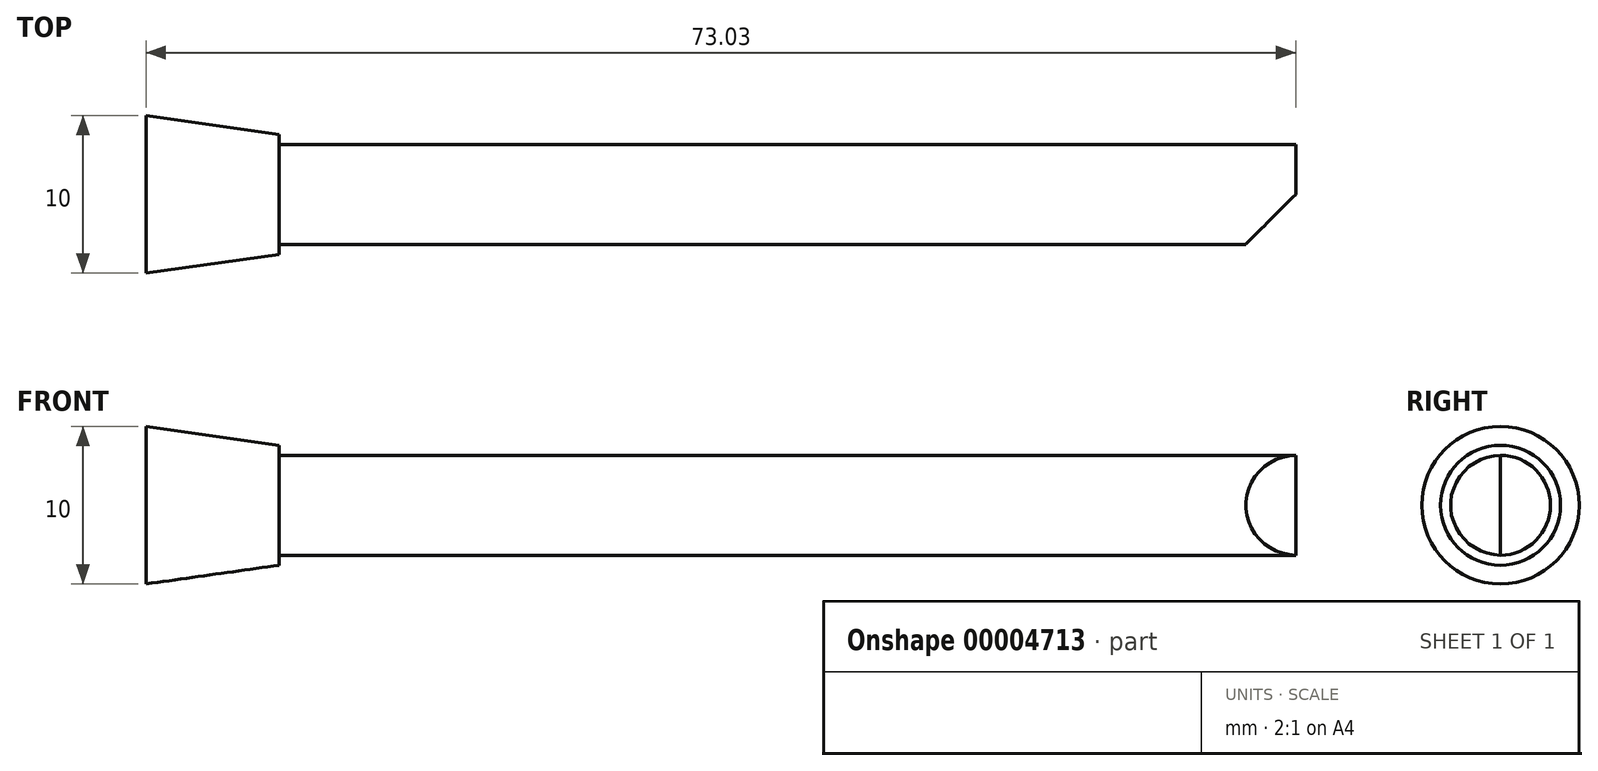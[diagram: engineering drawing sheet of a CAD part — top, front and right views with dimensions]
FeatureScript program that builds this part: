
annotation { "Feature Type Name" : "Feature", "Feature Type Description" : "" }
export const myFeature = defineFeature(function(context is Context, id is Id, definition is map)
    precondition{}
    {
        {
            var Q0;
            Q0=qCreatedBy(makeId("Top.planeOp"),FACE);
            var sketch = newSketch(context, id + "F0", { "sketchPlane" : qUnion([Q0])});
            skLineSegment(sketch, "E0.bottom", {"start": v(0, 0) * mm, "end": v(-76.2, 0) * mm});
            skLineSegment(sketch, "E0.top", {"start": v(0, 3.18) * mm, "end": v(-76.2, 3.18) * mm});
            skLineSegment(sketch, "E0.left", {"start": v(0, 0) * mm, "end": v(0, 3.18) * mm});
            skLineSegment(sketch, "E0.right", {"start": v(-76.2, 0) * mm, "end": v(-76.2, 3.18) * mm});
            skLineSegment(sketch, "E1.MirrorCS", {"start": v(-76.2, 0) * mm, "end": v(-76.2, -3.17) * mm});
            skLineSegment(sketch, "E2.MirrorCS", {"start": v(0, 0) * mm, "end": v(0, -3.17) * mm});
            skLineSegment(sketch, "E3.MirrorCS", {"start": v(0, -3.17) * mm, "end": v(-76.2, -3.17) * mm});
            skLineSegment(sketch, "E4", {"start": v(-67.73, 3.81) * mm, "end": v(-67.73, -3.81) * mm});
            skLineSegment(sketch, "E5", {"start": v(-67.73, -3.81) * mm, "end": v(-76.2, -5) * mm});
            skLineSegment(sketch, "E6", {"start": v(-76.2, -5) * mm, "end": v(-76.2, 5) * mm});
            skLineSegment(sketch, "E7", {"start": v(-76.2, 5) * mm, "end": v(-67.73, 3.81) * mm});
            skSolve(sketch);
        }
        {
            var Q0;
            Q0=makeQuery(id+"F0.imprint","IMPRINT",FACE,{"disambiguationData":[TD([[makeQuery(id+"F0.imprint","IMPRINT",EDGE,{"derivedFrom":sQuery(id+"F0.wireOp",EDGE,"E0.bottom")}),-1.0]])]});
            var Q1;
            {var subQ5=sQuery(id+"F0.wireOp",EDGE,"E7");Q1=makeQuery(id+"F0.imprint","IMPRINT",FACE,{"disambiguationData":[TD([[makeQuery(id+"F0.imprint","IMPRINT",EDGE,{"derivedFrom":subQ5}),-1.0]])]});}
            var Q2;
            Q2=sQuery(id+"F0.wireOp",EDGE,"E0.bottom");
            revolve(context, id + "F1", {"entities" : qUnion([Q0, Q1]), "axis" : qUnion([Q2]), "revolveType" : RevolveType.FULL});
        }
        {
            var Q0;
            Q0=qCreatedBy(makeId("Top.planeOp"),FACE);
            var sketch = newSketch(context, id + "F2", { "sketchPlane" : qUnion([Q0])});
            skLineSegment(sketch, "E8", {"start": v(0, 3.18) * mm, "end": v(-6.35, -3.17) * mm});
            skLineSegment(sketch, "E9", {"start": v(-6.35, -3.18) * mm, "end": v(0, -3.18) * mm});
            skLineSegment(sketch, "E10", {"start": v(0, -3.17) * mm, "end": v(0, 3.18) * mm});
            skLineSegment(sketch, "E11", {"start": v(-3.18, 0) * mm, "end": v(-3.18, 3.18) * mm});
            skLineSegment(sketch, "E12", {"start": v(-3.18, 3.18) * mm, "end": v(0, 3.18) * mm});
            skSolve(sketch);
        }
        {
            var Q0;
            Q0=makeQuery(id+"F2.imprint","IMPRINT",FACE,{"disambiguationData":[TD([[makeQuery(id+"F2.imprint","IMPRINT",EDGE,{"derivedFrom":sQuery(id+"F2.wireOp",EDGE,"E8")}),1.0]])]});
            var Q1;
            {var subQ2=sQuery(id+"F2.wireOp",EDGE,"E11");Q1=makeQuery(id+"F2.imprint","IMPRINT",FACE,{"disambiguationData":[TD([[makeQuery(id+"F2.imprint","IMPRINT",EDGE,{"derivedFrom":subQ2}),-1.0]])]});}
            extrude(context, id + "F3", {"entities" : qUnion([Q0, Q1]), "operationType" : NewBodyOperationType.REMOVE, "endBound" : BoundingType.THROUGH_ALL, "oppositeDirection" : true, "depth" : 25.4 * mm, "hasSecondDirection" : true, "secondDirectionOppositeDirection" : false, "secondDirectionDepth" : 25.4 * mm});
        }
    });
